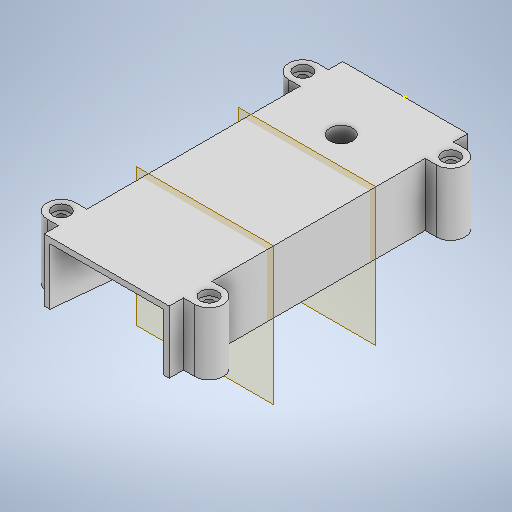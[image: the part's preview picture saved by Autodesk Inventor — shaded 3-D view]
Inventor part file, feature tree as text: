
AUTODESK INVENTOR PART (.ipt)
format: ipt  version: 2025.4 (Build 294407000, 407)  size: 407,552 bytes
history: native  units: mm
features: sketch x13, other x8, extrude x7, loft x2, hole x1
ambient origin geometry x8: Origin, YZ Plane, XZ Plane, XY Plane, X Axis, Y Axis, Z Axis, Center Point
bodies: Body1 (feature_tree)
feature tree (31):
  other  "Bryła1"
  other  "Płaszczyzna konstrukcyjna3"
  other  "Płaszczyzna konstrukcyjna4"
  other  "Płaszczyzna konstrukcyjna5"
  sketch  "Szkic7"
  sketch  "Szkic9"
  sketch  "Szkic10"
  sketch  "Szkic11"
  extrude  "Wyciągnięcie proste1"  Depth=35.0mm
  extrude  "Wyciągnięcie proste2"  Depth=38.0mm
  other  "Płaszczyzna konstrukcyjna6"
  other  "Płaszczyzna konstrukcyjna7"
  loft  "Wyciągnięcie złożone1"
  loft  "Wyciągnięcie złożone2"
  extrude  "Wyciągnięcie proste3"  Depth=40.0mm
  sketch  "Szkic14"
  extrude  "Wyciągnięcie proste4"  Depth=40.0mm
  extrude  "Wyciągnięcie proste5"  Depth=44.0mm
  sketch  "Szkic17"
  sketch  "Szkic18"
  extrude  "Wyciągnięcie proste6"  Depth=44.0mm
  hole  "Otwór1"  [1 undecoded]
  extrude  "Wyciągnięcie proste7"  Depth=35.5mm TaperAngle=0.0deg
  sketch  "Szkic12"
  other  "Krawędzie1"
  other  "Krawędzie2"
  sketch  "Szkic13"
  sketch  "Szkic15"
  sketch  "Szkic16"
  sketch  "Szkic19"
  sketch  "Szkic20"
note: 1 required parameter value undecoded (feature->parameter linkage not recoverable at this tier; creation-order binding heuristic only, values carry confidence <= 0.55)
